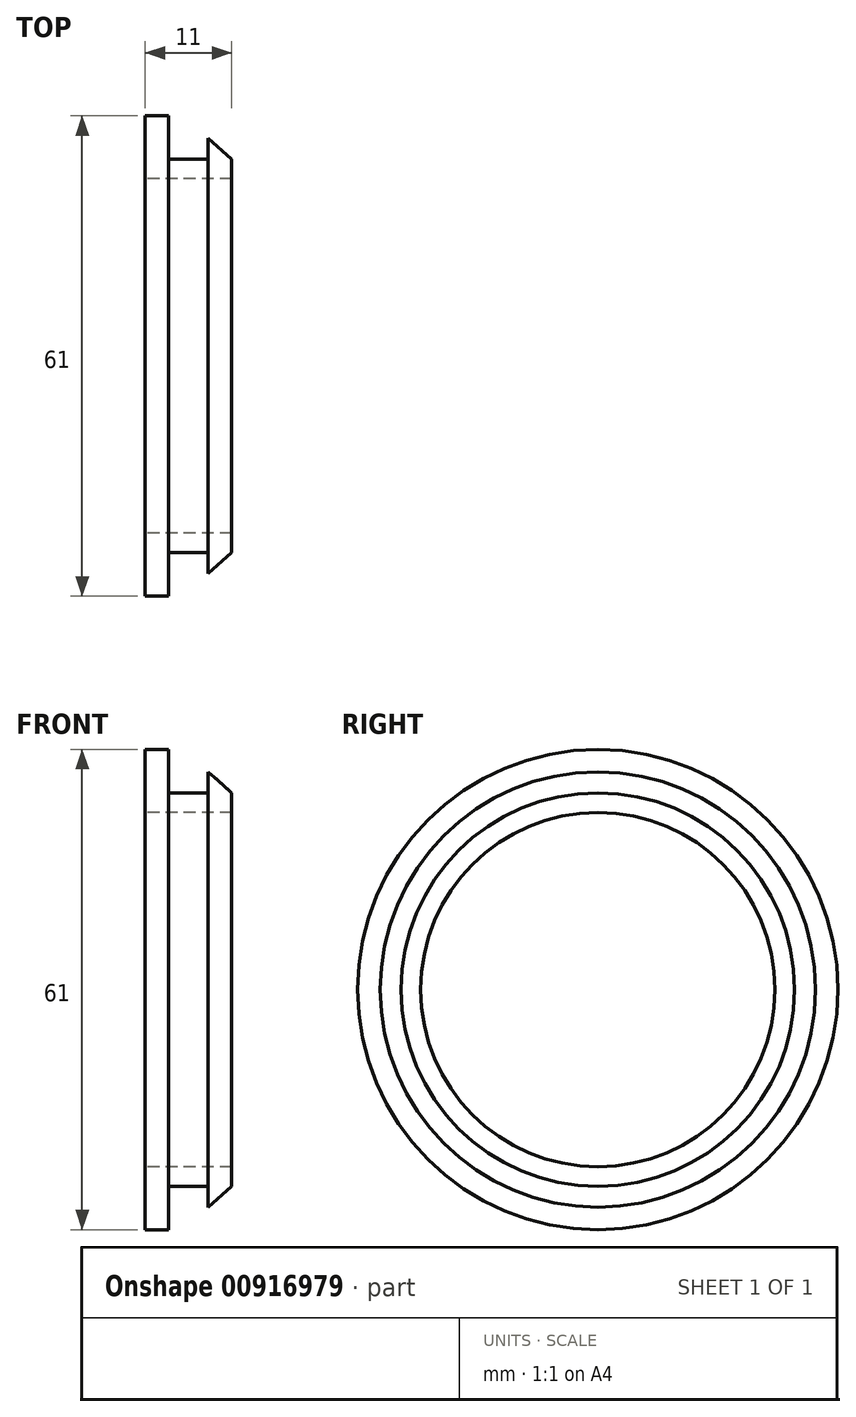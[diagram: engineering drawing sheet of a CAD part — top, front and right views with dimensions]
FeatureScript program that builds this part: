
annotation { "Feature Type Name" : "Feature", "Feature Type Description" : "" }
export const myFeature = defineFeature(function(context is Context, id is Id, definition is map)
    precondition{}
    {
        {
            var Q0;
            Q0=qCreatedBy(makeId("Front.planeOp"),FACE);
            var sketch = newSketch(context, id + "F0", { "sketchPlane" : qUnion([Q0])});
            skLineSegment(sketch, "E0", {"start": v(0, 0) * mm, "end": v(32.61, 0) * mm, "construction": true});
            skLineSegment(sketch, "E1", {"start": v(0, 22.5) * mm, "end": v(11, 22.5) * mm});
            skLineSegment(sketch, "E2", {"start": v(11, 22.5) * mm, "end": v(11, 25) * mm});
            skLineSegment(sketch, "E3", {"start": v(11, 25) * mm, "end": v(8, 27.65) * mm});
            skLineSegment(sketch, "E4", {"start": v(8, 27.65) * mm, "end": v(8, 25) * mm});
            skLineSegment(sketch, "E5", {"start": v(8, 25) * mm, "end": v(3, 25) * mm});
            skLineSegment(sketch, "E6", {"start": v(3, 25) * mm, "end": v(3, 30.5) * mm});
            skLineSegment(sketch, "E7", {"start": v(3, 30.5) * mm, "end": v(0, 30.5) * mm});
            skLineSegment(sketch, "E8", {"start": v(0, 30.5) * mm, "end": v(0, 22.5) * mm});
            skSolve(sketch);
        }
        {
            var Q0;
            Q0=makeQuery(id+"F0.imprint","IMPRINT",FACE,{"disambiguationData":[TD([[makeQuery(id+"F0.imprint","IMPRINT",EDGE,{"derivedFrom":sQuery(id+"F0.wireOp",EDGE,"E1")}),1.0]])]});
            var Q1;
            Q1=sQuery(id+"F0.wireOp",EDGE,"E0");
            revolve(context, id + "F1", {"surfaceOperationType" : NewSurfaceOperationType.NEW, "entities" : qUnion([Q0]), "axis" : qUnion([Q1]), "revolveType" : RevolveType.FULL});
        }
    });
